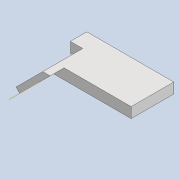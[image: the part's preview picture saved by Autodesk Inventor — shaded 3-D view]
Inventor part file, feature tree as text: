
AUTODESK INVENTOR PART (.ipt)
format: ipt  version: 2020 (Build 240168000, 168)  size: 228,352 bytes
history: native  units: mm
features: fillet x7, sketch x6, extrude x6, other x5, projected_geometry x4, reference x3, plane x2, chamfer x1, thicken_offset x1
ambient origin geometry x8: Origin, YZ Plane, XZ Plane, XY Plane, X Axis, Y Axis, Z Axis, Center Point
bodies: Solid1 (feature_tree)
feature tree (35):
  sketch  "Sketch1"  dims[d0=10.0mm d1=0.0mm d2=18.0mm d3=0.0mm]
  plane  "Work Plane1"
  extrude  "Extrusion1"  Depth=10.0mm TaperAngle=0.0deg
  extrude  "Extrusion2"  Depth=2.0mm
  plane  "Work Plane2"
  extrude  "Extrusion3"  Depth=20.0mm
  extrude  "Extrusion4"  Depth=3.0mm TaperAngle=0.0deg
  extrude  "Extrusion5"  Depth=15.0mm TaperAngle=0.0deg
  extrude  "Extrusion6"  Depth=8.0mm
  fillet  "Fillet1"  Radius=15.0mm
  fillet  "Fillet2"  Radius=2.0mm
  fillet  "Fillet3"  Radius=6.0mm
  fillet  "Fillet4"  Radius=2.0mm
  fillet  "Fillet5"  Radius=4.0mm
  fillet  "Fillet6"  Radius=1.0mm
  fillet  "Fillet7"  Radius=3.0mm
  chamfer  "Chamfer1"  Distance=3.0mm
  thicken_offset  "Thicken1"
  reference  "Reference1"
  sketch  "Sketch2"  dims[d4=2.0mm d5=2.0mm]
  projected_geometry  "Projected Loop1"
  sketch  "Sketch3"  dims[d6=5.0mm d7=20.0mm]
  reference  "Reference2"
  sketch  "Sketch4"  dims[d8=8.0mm d9=3.0mm d10=0.0mm]
  projected_geometry  "Projected Loop2"
  sketch  "Sketch5"  dims[d11=3.0mm d12=0.0mm d13=15.0mm d14=0.0mm]
  projected_geometry  "Projected Loop3"
  sketch  "Sketch6"  dims[d15=20.0mm d16=8.0mm d17=15.0mm d18=0.0mm d19=2.0mm d20=6.0mm d21=2.0mm d22=4.0mm d23=1.0mm d24=3.0mm d25=3.0mm d26=2.0mm d27=2.0mm d28=45.0deg d29=8.0mm d30=8.0mm]
  reference  "Reference3"
  projected_geometry  "Projected Loop4"
  parser-record x1  (decoder bookkeeping rows leaked as tree rows — omitted from the tree; the rows remain in map.json)
  other  "driver_unit_1.iam"
  other  "drv_stand_1:1"
  other  "mot_holder_1:1"
  other  "tendon_wh_3:1"
note: 1 file-system path scrubbed to <path> (originals preserved in map.json)
